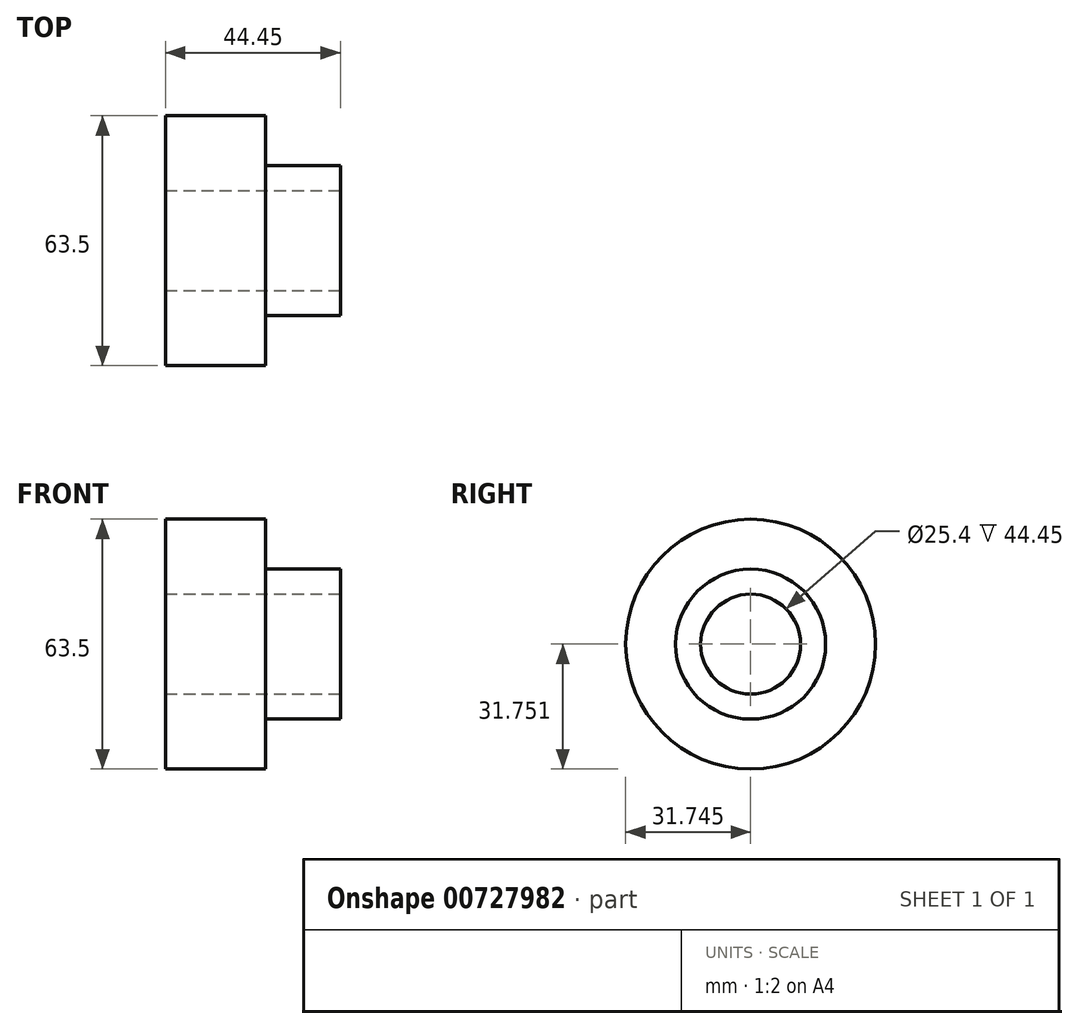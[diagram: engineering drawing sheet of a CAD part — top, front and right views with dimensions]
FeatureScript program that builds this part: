
annotation { "Feature Type Name" : "Feature", "Feature Type Description" : "" }
export const myFeature = defineFeature(function(context is Context, id is Id, definition is map)
    precondition{}
    {
        {
            var Q0;
            Q0=qCreatedBy(makeId("Right.planeOp"),FACE);
            var sketch = newSketch(context, id + "F0", { "sketchPlane" : qUnion([Q0])});
            skCircle(sketch, "E0", {"center": v(-16.16, 25.7) * mm, "radius": 31.75 * mm});
            skSolve(sketch);
        }
        {
            var Q0;
            Q0=makeQuery(id+"F0.imprint","IMPRINT",FACE,{"disambiguationData":[TD([[makeQuery(id+"F0.imprint","IMPRINT",EDGE,{"derivedFrom":sQuery(id+"F0.wireOp",EDGE,"E0")}),1.0]])]});
            extrude(context, id + "F1", {"entities" : qUnion([Q0]), "depth" : 25.4 * mm, "offsetDistance" : 25.4 * mm});
        }
        {
            var Q0;
            Q0=makeQuery(id+"F1.opExtrude","CAP_FACE",FACE,{"disambiguationData":[OSD([sQuery(id+"F0.wireOp",EDGE,"E0")])],"isStart":false});
            var sketch = newSketch(context, id + "F2", { "sketchPlane" : qUnion([Q0])});
            skCircle(sketch, "E1", {"center": v(-16.16, 25.7) * mm, "radius": 19.05 * mm});
            skSolve(sketch);
        }
        {
            var Q0;
            Q0=makeQuery(id+"F2.imprint","IMPRINT",FACE,{"disambiguationData":[TD([[makeQuery(id+"F2.imprint","IMPRINT",EDGE,{"derivedFrom":sQuery(id+"F2.wireOp",EDGE,"E1")}),1.0]])]});
            extrude(context, id + "F3", {"entities" : qUnion([Q0]), "operationType" : NewBodyOperationType.ADD, "depth" : 19.05 * mm, "offsetDistance" : 25.4 * mm});
        }
        {
            var Q0;
            Q0=makeQuery(id+"F3.opExtrude","CAP_FACE",FACE,{"disambiguationData":[OSD([sQuery(id+"F2.wireOp",EDGE,"E1")])],"isStart":false});
            var sketch = newSketch(context, id + "F4", { "sketchPlane" : qUnion([Q0])});
            skCircle(sketch, "E2", {"center": v(-16.16, 25.7) * mm, "radius": 12.7 * mm});
            skSolve(sketch);
        }
        {
            var Q0;
            Q0=makeQuery(id+"F4.imprint","IMPRINT",FACE,{"disambiguationData":[TD([[makeQuery(id+"F4.imprint","IMPRINT",EDGE,{"derivedFrom":sQuery(id+"F4.wireOp",EDGE,"E2")}),1.0]])]});
            extrude(context, id + "F5", {"entities" : qUnion([Q0]), "operationType" : NewBodyOperationType.REMOVE, "endBound" : BoundingType.THROUGH_ALL, "oppositeDirection" : true, "depth" : 25.4 * mm, "offsetDistance" : 25.4 * mm});
        }
    });
